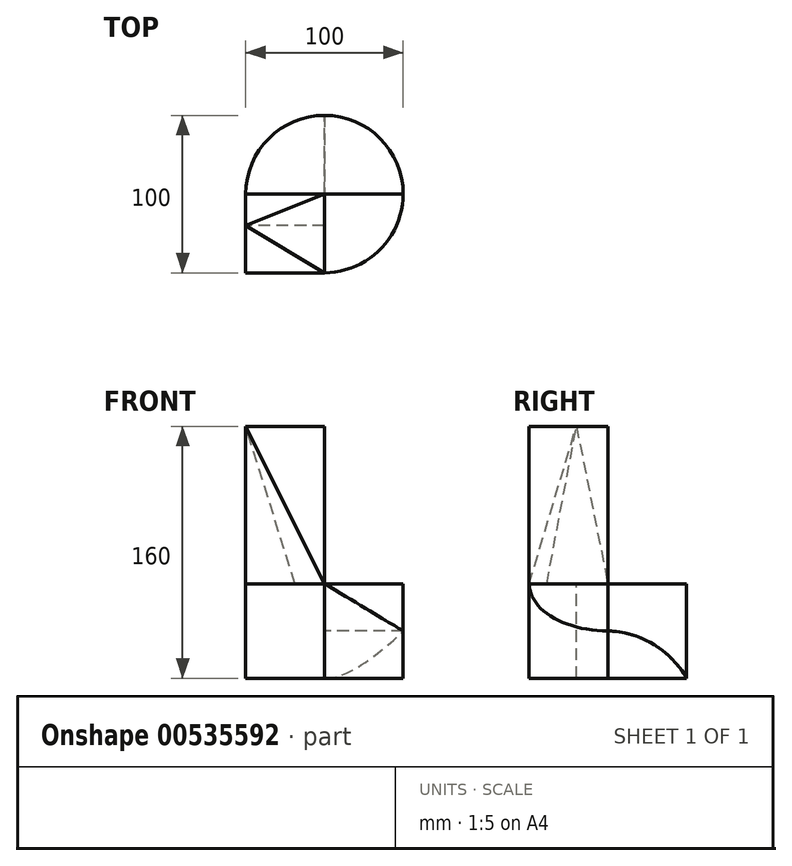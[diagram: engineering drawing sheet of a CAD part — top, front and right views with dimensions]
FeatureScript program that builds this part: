
annotation { "Feature Type Name" : "Feature", "Feature Type Description" : "" }
export const myFeature = defineFeature(function(context is Context, id is Id, definition is map)
    precondition{}
    {
        {
            var Q0;
            Q0=qCreatedBy(makeId("Top.planeOp"),FACE);
            var sketch = newSketch(context, id + "F0", { "sketchPlane" : qUnion([Q0])});
            skCircle(sketch, "E0", {"center": v(0, 0) * mm, "radius": 50 * mm});
            skSolve(sketch);
        }
        {
            var Q0;
            Q0=makeQuery(id+"F0.imprint","IMPRINT",FACE,{"disambiguationData":[TD([[makeQuery(id+"F0.imprint","IMPRINT",EDGE,{"derivedFrom":sQuery(id+"F0.wireOp",EDGE,"E0")}),1.0]])]});
            extrude(context, id + "F1", {"entities" : qUnion([Q0]), "depth" : 60 * mm, "offsetDistance" : 25 * mm});
        }
        {
            var Q0;
            Q0=makeQuery(id+"F1.opExtrude","CAP_FACE",FACE,{"disambiguationData":[OSD([sQuery(id+"F0.wireOp",EDGE,"E0")])],"isStart":true});
            var sketch = newSketch(context, id + "F2", { "sketchPlane" : qUnion([Q0])});
            skLineSegment(sketch, "E1.bottom", {"start": v(0, 0) * mm, "end": v(-50, 0) * mm});
            skLineSegment(sketch, "E1.top", {"start": v(0, 50) * mm, "end": v(-50, 50) * mm});
            skLineSegment(sketch, "E1.left", {"start": v(0, 0) * mm, "end": v(0, 50) * mm});
            skLineSegment(sketch, "E1.right", {"start": v(-50, 0) * mm, "end": v(-50, 50) * mm});
            skSolve(sketch);
        }
        {
            var Q0;
            {var subQ0=sQuery(id+"F2.wireOp",EDGE,"E1.bottom");Q0=makeQuery(id+"F2.imprint","IMPRINT",FACE,{"disambiguationData":[TD([[makeQuery(id+"F2.imprint","IMPRINT",EDGE,{"derivedFrom":subQ0}),-1.0]])]});}
            extrude(context, id + "F3", {"entities" : qUnion([Q0]), "operationType" : NewBodyOperationType.REMOVE, "endBound" : BoundingType.THROUGH_ALL, "oppositeDirection" : true, "depth" : 25 * mm, "offsetDistance" : 25 * mm});
        }
        {
            var Q0;
            {var subQ0=sQuery(id+"F2.wireOp",EDGE,"E1.top");Q0=makeQuery(id+"F2.imprint","IMPRINT",FACE,{"disambiguationData":[TD([[makeQuery(id+"F2.imprint","IMPRINT",EDGE,{"derivedFrom":subQ0}),1.0]])]});}
            var Q1;
            {var subQ0=sQuery(id+"F2.wireOp",EDGE,"E1.bottom");Q1=makeQuery(id+"F2.imprint","IMPRINT",FACE,{"disambiguationData":[TD([[makeQuery(id+"F2.imprint","IMPRINT",EDGE,{"derivedFrom":subQ0}),-1.0]])]});}
            extrude(context, id + "F4", {"entities" : qUnion([Q0, Q1]), "operationType" : NewBodyOperationType.ADD, "oppositeDirection" : true, "depth" : 160 * mm, "offsetDistance" : 25 * mm});
        }
        {
            var Q0;
            Q0=makeQuery(id+"F4.opExtrude","SWEPT_FACE",FACE,{"disambiguationData":[OSD([sQuery(id+"F2.wireOp",EDGE,"E1.right")])]});
            var sketch = newSketch(context, id + "F5", { "sketchPlane" : qUnion([Q0])});
            skLineSegment(sketch, "E2.bottom", {"start": v(50, 0) * mm, "end": v(20, 0) * mm});
            skLineSegment(sketch, "E2.top", {"start": v(50, 60) * mm, "end": v(20, 60) * mm});
            skLineSegment(sketch, "E2.left", {"start": v(50, 0) * mm, "end": v(50, 60) * mm});
            skLineSegment(sketch, "E2.right", {"start": v(20, 0) * mm, "end": v(20, 60) * mm});
            skSolve(sketch);
        }
        {
            var Q0;
            Q0=makeQuery(id+"F5.imprint","IMPRINT",FACE,{"disambiguationData":[TD([[makeQuery(id+"F5.imprint","IMPRINT",EDGE,{"derivedFrom":sQuery(id+"F5.wireOp",EDGE,"E2.bottom")}),1.0]])]});
            extrude(context, id + "F6", {"entities" : qUnion([Q0]), "operationType" : NewBodyOperationType.REMOVE, "oppositeDirection" : true, "depth" : 50 * mm, "offsetDistance" : 25 * mm});
        }
        {
            var Q0;
            Q0=makeQuery(id+"F4.opExtrude","CAP_FACE",FACE,{"disambiguationData":[OSD([sQuery(id+"F2.wireOp",EDGE,"E1.bottom"),sQuery(id+"F2.wireOp",EDGE,"E1.top"),sQuery(id+"F2.wireOp",EDGE,"E1.left"),sQuery(id+"F2.wireOp",EDGE,"E1.right")])],"isStart":false});
            var sketch = newSketch(context, id + "F7", { "sketchPlane" : qUnion([Q0])});
            skLineSegment(sketch, "E3", {"start": v(-50, -50) * mm, "end": v(-50, -20) * mm});
            skLineSegment(sketch, "E4", {"start": v(-50, -20) * mm, "end": v(-50, 0) * mm});
            skLineSegment(sketch, "E5", {"start": v(-50, -20) * mm, "end": v(0, 0) * mm});
            skLineSegment(sketch, "E6", {"start": v(0, 0) * mm, "end": v(0, -50) * mm});
            skLineSegment(sketch, "E7", {"start": v(0, -50) * mm, "end": v(-50, -20) * mm});
            skLineSegment(sketch, "E8", {"start": v(-50, -20) * mm, "end": v(0, -20) * mm});
            skSolve(sketch);
        }
        {
            var Q0;
            Q0=makeQuery(id+"F4.opExtrude","SWEPT_FACE",FACE,{"disambiguationData":[OSD([sQuery(id+"F2.wireOp",EDGE,"E1.right")])]});
            var sketch = newSketch(context, id + "F8", { "sketchPlane" : qUnion([Q0])});
            skLineSegment(sketch, "E9", {"start": v(20, 160) * mm, "end": v(20, 60.2) * mm});
            skSolve(sketch);
        }
        {
            var Q1;
            Q1=makeQuery(id+"F4.opExtrude","SWEPT_FACE",FACE,{"disambiguationData":[OSD([sQuery(id+"F2.wireOp",EDGE,"E1.top")])]});
            var Q2;
            Q2=sQuery(id+"F8.wireOp",VERTEX,"E9.start");
            loft(context, id + "F9", {"operationType" : NewBodyOperationType.REMOVE, "sheetProfilesArray" : [{ "sheetProfileEntities" : qUnion([Q1]) }, { "sheetProfileEntities" : qUnion([Q2]) }]});
        }
        {
            var Q1;
            Q1=makeQuery(id+"F7.imprint","IMPRINT",FACE,{"disambiguationData":[TD([[makeQuery(id+"F7.imprint","IMPRINT",EDGE,{"derivedFrom":sQuery(id+"F7.wireOp",EDGE,"E4")}),1.0]])]});
            var Q2;
            Q2=makeQuery(id+"F3.boolean.opBoolean","INTERSECT",VERTEX,{"derivedFrom":[makeQuery(id+"F1.opExtrude","CAP_FACE",FACE,{"disambiguationData":[OSD([sQuery(id+"F0.wireOp",EDGE,"E0")])],"isStart":false}),makeQuery(id+"F3.opExtrude","SWEPT_FACE",FACE,{"disambiguationData":[OSD([sQuery(id+"F2.wireOp",EDGE,"E1.bottom")])]}),makeQuery(id+"F3.opExtrude","SWEPT_FACE",FACE,{"disambiguationData":[OSD([sQuery(id+"F2.wireOp",EDGE,"E1.left")])]})]});
            loft(context, id + "F10", {"operationType" : NewBodyOperationType.REMOVE, "sheetProfilesArray" : [{ "sheetProfileEntities" : qUnion([Q1]) }, { "sheetProfileEntities" : qUnion([Q2]) }]});
        }
        {
            var Q0;
            Q0=makeQuery(id+"F1.opExtrude","CAP_FACE",FACE,{"disambiguationData":[OSD([sQuery(id+"F0.wireOp",EDGE,"E0")])],"isStart":false});
            var sketch = newSketch(context, id + "F11", { "sketchPlane" : qUnion([Q0])});
            skLineSegment(sketch, "E10", {"start": v(0, 0) * mm, "end": v(50, 0) * mm});
            skSolve(sketch);
        }
        {
            var Q0;
            Q0=qCreatedBy(makeId("Front.planeOp"),FACE);
            var sketch = newSketch(context, id + "F12", { "sketchPlane" : qUnion([Q0])});
            skLineSegment(sketch, "E11", {"start": v(0, 0) * mm, "end": v(0, 30) * mm});
            skLineSegment(sketch, "E12", {"start": v(0, 30) * mm, "end": v(0, 60) * mm});
            skLineSegment(sketch, "E13", {"start": v(0, 30) * mm, "end": v(50, 60) * mm});
            skLineSegment(sketch, "E14", {"start": v(50, 60) * mm, "end": v(0, 60) * mm});
            skLineSegment(sketch, "E15", {"start": v(50, 60) * mm, "end": v(50, 30) * mm});
            skLineSegment(sketch, "E16", {"start": v(50, 30) * mm, "end": v(0, 30) * mm});
            skLineSegment(sketch, "E17", {"start": v(50, 30) * mm, "end": v(0, 60) * mm});
            skSolve(sketch);
        }
        {
            var Q0;
            {var subQ0=sQuery(id+"F12.wireOp",EDGE,"E15");Q0=makeQuery(id+"F12.imprint","IMPRINT",FACE,{"disambiguationData":[TD([[makeQuery(id+"F12.imprint","IMPRINT",EDGE,{"derivedFrom":subQ0}),-1.0]])]});}
            var Q1;
            {var subQ0=sQuery(id+"F12.wireOp",EDGE,"E14");Q1=makeQuery(id+"F12.imprint","IMPRINT",FACE,{"disambiguationData":[TD([[makeQuery(id+"F12.imprint","IMPRINT",EDGE,{"derivedFrom":subQ0}),1.0]])]});}
            extrude(context, id + "F13", {"entities" : qUnion([Q0, Q1]), "operationType" : NewBodyOperationType.REMOVE, "depth" : 50 * mm, "offsetDistance" : 25 * mm});
        }
        {
            var Q0;
            Q0=qCreatedBy(makeId("Right.planeOp"),FACE);
            var sketch = newSketch(context, id + "F14", { "sketchPlane" : qUnion([Q0])});
            skLineSegment(sketch, "E18.bottom", {"start": v(0, 0) * mm, "end": v(50, 0) * mm});
            skLineSegment(sketch, "E18.top", {"start": v(0, 60) * mm, "end": v(50, 60) * mm});
            skLineSegment(sketch, "E18.left", {"start": v(0, 0) * mm, "end": v(0, 60) * mm});
            skLineSegment(sketch, "E18.right", {"start": v(50, 0) * mm, "end": v(50, 60) * mm});
            skArc(sketch, "E19", {"start": v(50, 0) * mm, "mid": v(28.89, 21.48) * mm, "end": v(0, 30) * mm});
            skLineSegment(sketch, "E20", {"start": v(0, 30) * mm, "end": v(0, 0) * mm});
            skSolve(sketch);
        }
        {
            var Q0;
            Q0=makeQuery(id+"F14.imprint","IMPRINT",FACE,{"disambiguationData":[TD([[makeQuery(id+"F14.imprint","IMPRINT",EDGE,{"derivedFrom":sQuery(id+"F14.wireOp",EDGE,"E19")}),1.0]])]});
            extrude(context, id + "F15", {"entities" : qUnion([Q0]), "operationType" : NewBodyOperationType.REMOVE, "endBound" : BoundingType.THROUGH_ALL, "depth" : 25 * mm, "offsetDistance" : 25 * mm});
        }
    });
